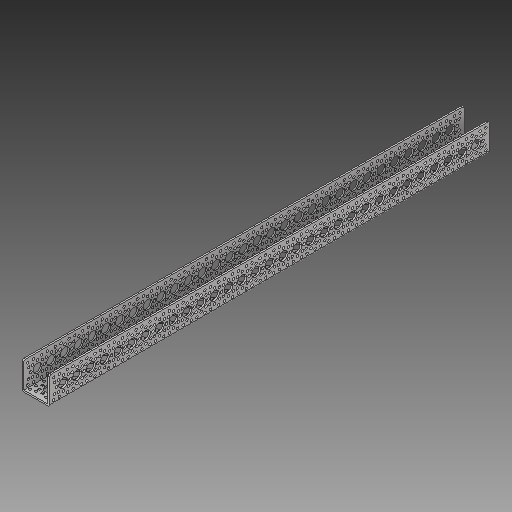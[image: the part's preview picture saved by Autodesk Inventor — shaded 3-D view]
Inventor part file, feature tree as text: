
AUTODESK INVENTOR PART (.ipt)
format: ipt  version: 2017 (Build 210142000, 142)  size: 1,270,784 bytes
history: native  units: in
note: dims shown in document units (in); Inventor stores cm internally (conversion verified against a paired STEP export)
features: fillet x1
ambient origin geometry x8: Origin, YZ Plane, XZ Plane, XY Plane, X Axis, Y Axis, Z Axis, Center Point
bodies: Solid1 (feature_tree)
feature tree (1):
  fillet  "Fillet1"  [1 undecoded]
note: 1 required parameter value undecoded (feature->parameter linkage not recoverable at this tier; creation-order binding heuristic only, values carry confidence <= 0.55)
